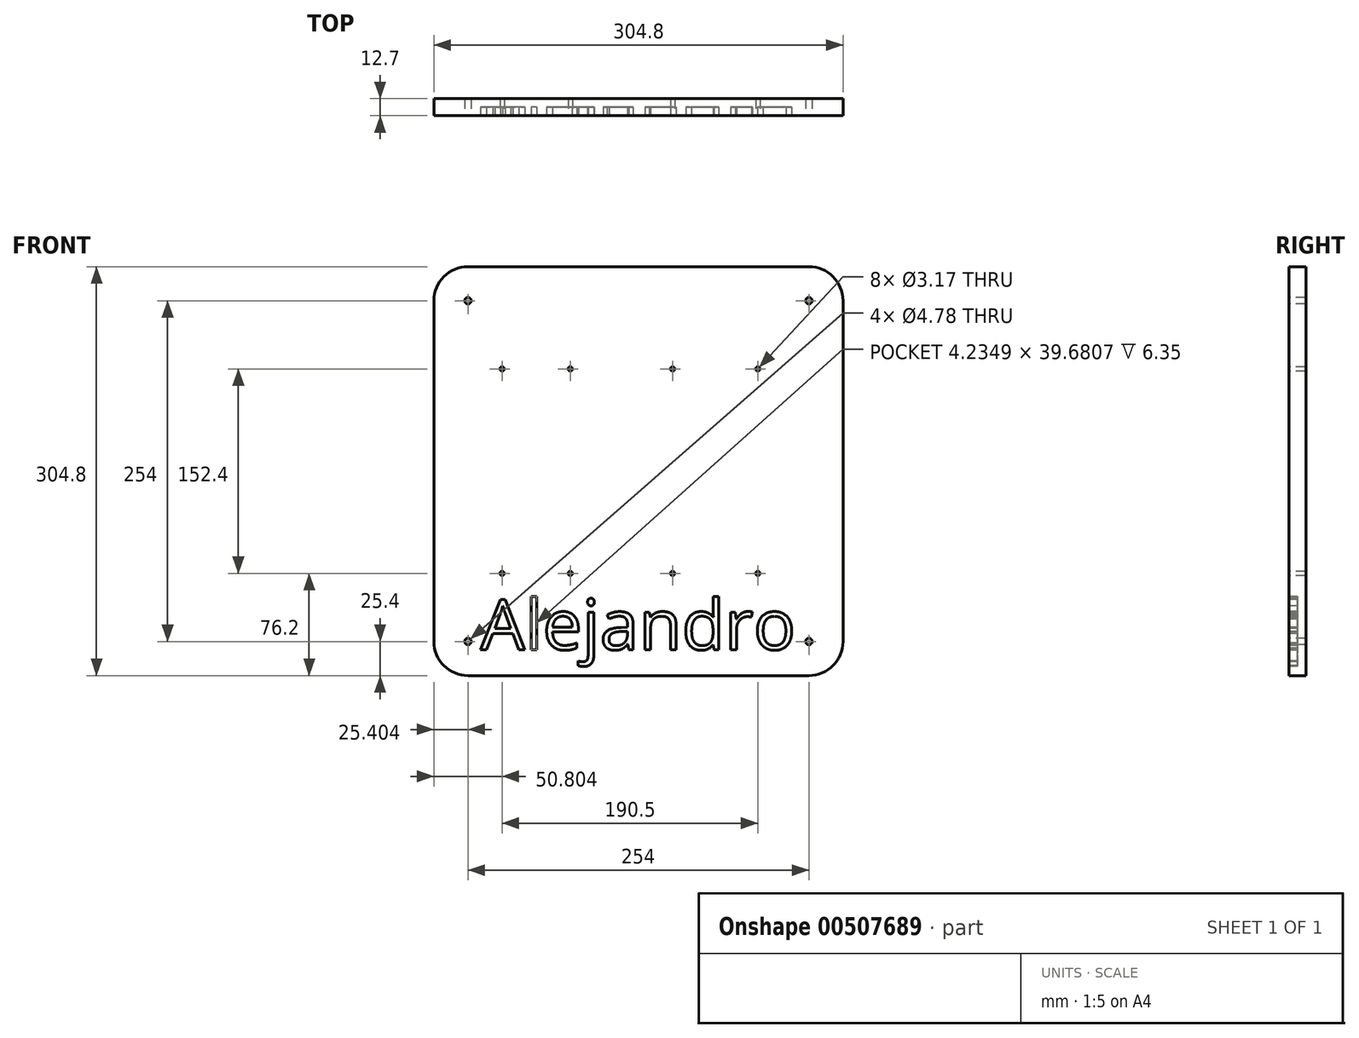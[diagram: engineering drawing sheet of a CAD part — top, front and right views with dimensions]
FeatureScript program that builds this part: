
annotation { "Feature Type Name" : "Feature", "Feature Type Description" : "" }
export const myFeature = defineFeature(function(context is Context, id is Id, definition is map)
    precondition{}
    {
        {
            var Q0;
            Q0=qCreatedBy(makeId("Front.planeOp"),FACE);
            var sketch = newSketch(context, id + "F0", { "sketchPlane" : qUnion([Q0])});
            skLineSegment(sketch, "E0.bottom", {"start": v(-8.43, 0) * mm, "end": v(296.37, 0) * mm});
            skLineSegment(sketch, "E0.top", {"start": v(-8.43, 304.8) * mm, "end": v(296.37, 304.8) * mm});
            skLineSegment(sketch, "E0.left", {"start": v(-8.43, 0) * mm, "end": v(-8.43, 304.8) * mm});
            skLineSegment(sketch, "E0.right", {"start": v(296.37, 0) * mm, "end": v(296.37, 304.8) * mm});
            skSolve(sketch);
        }
        {
            var Q0;
            Q0=makeQuery(id+"F0.imprint","IMPRINT",FACE,{"disambiguationData":[TD([[makeQuery(id+"F0.imprint","IMPRINT",EDGE,{"derivedFrom":sQuery(id+"F0.wireOp",EDGE,"E0.bottom")}),1.0]])]});
            extrude(context, id + "F1", {"entities" : qUnion([Q0]), "depth" : 12.7 * mm});
        }
        {
            var Q0;
            Q0=makeQuery(id+"F1.opExtrude","CAP_FACE",FACE,{"disambiguationData":[OSD([sQuery(id+"F0.wireOp",EDGE,"E0.bottom"),sQuery(id+"F0.wireOp",EDGE,"E0.top"),sQuery(id+"F0.wireOp",EDGE,"E0.left"),sQuery(id+"F0.wireOp",EDGE,"E0.right")])],"isStart":false});
            var sketch = newSketch(context, id + "F2", { "sketchPlane" : qUnion([Q0])});
            skPoint(sketch, "E1", {"position": v(42.37, 228.6) * mm});
            skPoint(sketch, "E2", {"position": v(93.17, 228.6) * mm});
            skPoint(sketch, "E3", {"position": v(169.37, 228.6) * mm});
            skPoint(sketch, "E4", {"position": v(232.87, 228.6) * mm});
            skPoint(sketch, "E5", {"position": v(42.37, 76.2) * mm});
            skPoint(sketch, "E6", {"position": v(93.17, 76.2) * mm});
            skPoint(sketch, "E7", {"position": v(169.37, 76.2) * mm});
            skPoint(sketch, "E8", {"position": v(232.87, 76.2) * mm});
            skSolve(sketch);
        }
        {
            var Q0;
            Q0=sQuery(id+"F2.wireOp",VERTEX,"E1");
            var Q1;
            Q1=sQuery(id+"F2.wireOp",VERTEX,"E2");
            var Q2;
            Q2=sQuery(id+"F2.wireOp",VERTEX,"E3");
            var Q3;
            Q3=sQuery(id+"F2.wireOp",VERTEX,"E4");
            var Q4;
            Q4=sQuery(id+"F2.wireOp",VERTEX,"E5");
            var Q5;
            Q5=sQuery(id+"F2.wireOp",VERTEX,"E6");
            var Q6;
            Q6=sQuery(id+"F2.wireOp",VERTEX,"E7");
            var Q7;
            Q7=sQuery(id+"F2.wireOp",VERTEX,"E8");
            var Q8;
            Q8=makeQuery(id+"F1.opExtrude","SWEPT_BODY",BODY,{"disambiguationData":[OSD([sQuery(id+"F0.wireOp",EDGE,"E0.bottom"),sQuery(id+"F0.wireOp",EDGE,"E0.top"),sQuery(id+"F0.wireOp",EDGE,"E0.left"),sQuery(id+"F0.wireOp",EDGE,"E0.right")])]});
            hole(context, id + "F3", {"style" : HoleStyle.SIMPLE, "endStyle" : HoleEndStyle.THROUGH, "holeDiameter" : 3.17 * mm, "isTappedThrough" : true, "tappedDepth" : 12.7 * mm, "tapClearance" : 3, "locations" : qUnion([Q0, Q1, Q2, Q3, Q4, Q5, Q6, Q7]), "scope" : qUnion([Q8])});
        }
        {
            var Q0;
            Q0=makeQuery(id+"F1.opExtrude","CAP_FACE",FACE,{"disambiguationData":[OSD([sQuery(id+"F0.wireOp",EDGE,"E0.bottom"),sQuery(id+"F0.wireOp",EDGE,"E0.top"),sQuery(id+"F0.wireOp",EDGE,"E0.left"),sQuery(id+"F0.wireOp",EDGE,"E0.right")])],"isStart":false});
            var sketch = newSketch(context, id + "F4", { "sketchPlane" : qUnion([Q0])});
            skPoint(sketch, "E9", {"position": v(16.97, 279.4) * mm});
            skPoint(sketch, "E10", {"position": v(16.97, 25.4) * mm});
            skPoint(sketch, "E11", {"position": v(270.97, 279.4) * mm});
            skPoint(sketch, "E12", {"position": v(270.97, 25.4) * mm});
            skSolve(sketch);
        }
        {
            var Q0;
            Q0=sQuery(id+"F4.wireOp",VERTEX,"E9");
            var Q1;
            Q1=sQuery(id+"F4.wireOp",VERTEX,"E11");
            var Q2;
            Q2=sQuery(id+"F4.wireOp",VERTEX,"E10");
            var Q3;
            Q3=sQuery(id+"F4.wireOp",VERTEX,"E12");
            var Q4;
            Q4=makeQuery(id+"F1.opExtrude","SWEPT_BODY",BODY,{"disambiguationData":[OSD([sQuery(id+"F0.wireOp",EDGE,"E0.bottom"),sQuery(id+"F0.wireOp",EDGE,"E0.top"),sQuery(id+"F0.wireOp",EDGE,"E0.left"),sQuery(id+"F0.wireOp",EDGE,"E0.right")])]});
            hole(context, id + "F5", {"style" : HoleStyle.SIMPLE, "endStyle" : HoleEndStyle.THROUGH, "holeDiameter" : 4.78 * mm, "isTappedThrough" : true, "tappedDepth" : 12.7 * mm, "tapClearance" : 3, "locations" : qUnion([Q0, Q1, Q2, Q3]), "scope" : qUnion([Q4])});
        }
        {
            var Q0;
            Q0=makeQuery(id+"F1.opExtrude","SWEPT_EDGE",EDGE,{"disambiguationData":[OSD([sQuery(id+"F0.wireOp",EDGE,"E0.top"),sQuery(id+"F0.wireOp",EDGE,"E0.left")])]});
            var Q1;
            Q1=makeQuery(id+"F1.opExtrude","SWEPT_EDGE",EDGE,{"disambiguationData":[OSD([sQuery(id+"F0.wireOp",EDGE,"E0.top"),sQuery(id+"F0.wireOp",EDGE,"E0.right")])]});
            var Q2;
            Q2=makeQuery(id+"F1.opExtrude","SWEPT_EDGE",EDGE,{"disambiguationData":[OSD([sQuery(id+"F0.wireOp",EDGE,"E0.bottom"),sQuery(id+"F0.wireOp",EDGE,"E0.right")])]});
            var Q3;
            Q3=makeQuery(id+"F1.opExtrude","SWEPT_EDGE",EDGE,{"disambiguationData":[OSD([sQuery(id+"F0.wireOp",EDGE,"E0.bottom"),sQuery(id+"F0.wireOp",EDGE,"E0.left")])]});
            fillet(context, id + "F6", {"entities" : qUnion([Q0, Q1, Q2, Q3]), "radius" : 25.4 * mm, "tangentPropagation" : true, "allowEdgeOverflow" : false});
        }
        {
            var Q0;
            Q0=makeQuery(id+"F1.opExtrude","CAP_FACE",FACE,{"disambiguationData":[OSD([sQuery(id+"F0.wireOp",EDGE,"E0.bottom"),sQuery(id+"F0.wireOp",EDGE,"E0.top"),sQuery(id+"F0.wireOp",EDGE,"E0.left"),sQuery(id+"F0.wireOp",EDGE,"E0.right")])],"isStart":false});
            var sketch = newSketch(context, id + "F7", { "sketchPlane" : qUnion([Q0])});
            skText(sketch, "E13", { "text": "Alejandro ", "fontName": "OpenSans-Regular.ttf"});
            const initialGuessF7  = {"E13": [0.0264, 0.01933, 1, 0, 0.0376]};
            skSetInitialGuess(sketch, initialGuessF7);
            skSolve(sketch);
        }
        {
            var Q0;
            Q0 = qSketchRegion(id + "F7", true);
            extrude(context, id + "F8", {"entities" : qUnion([Q0]), "operationType" : NewBodyOperationType.REMOVE, "oppositeDirection" : true, "depth" : 6.35 * mm});
        }
    });
